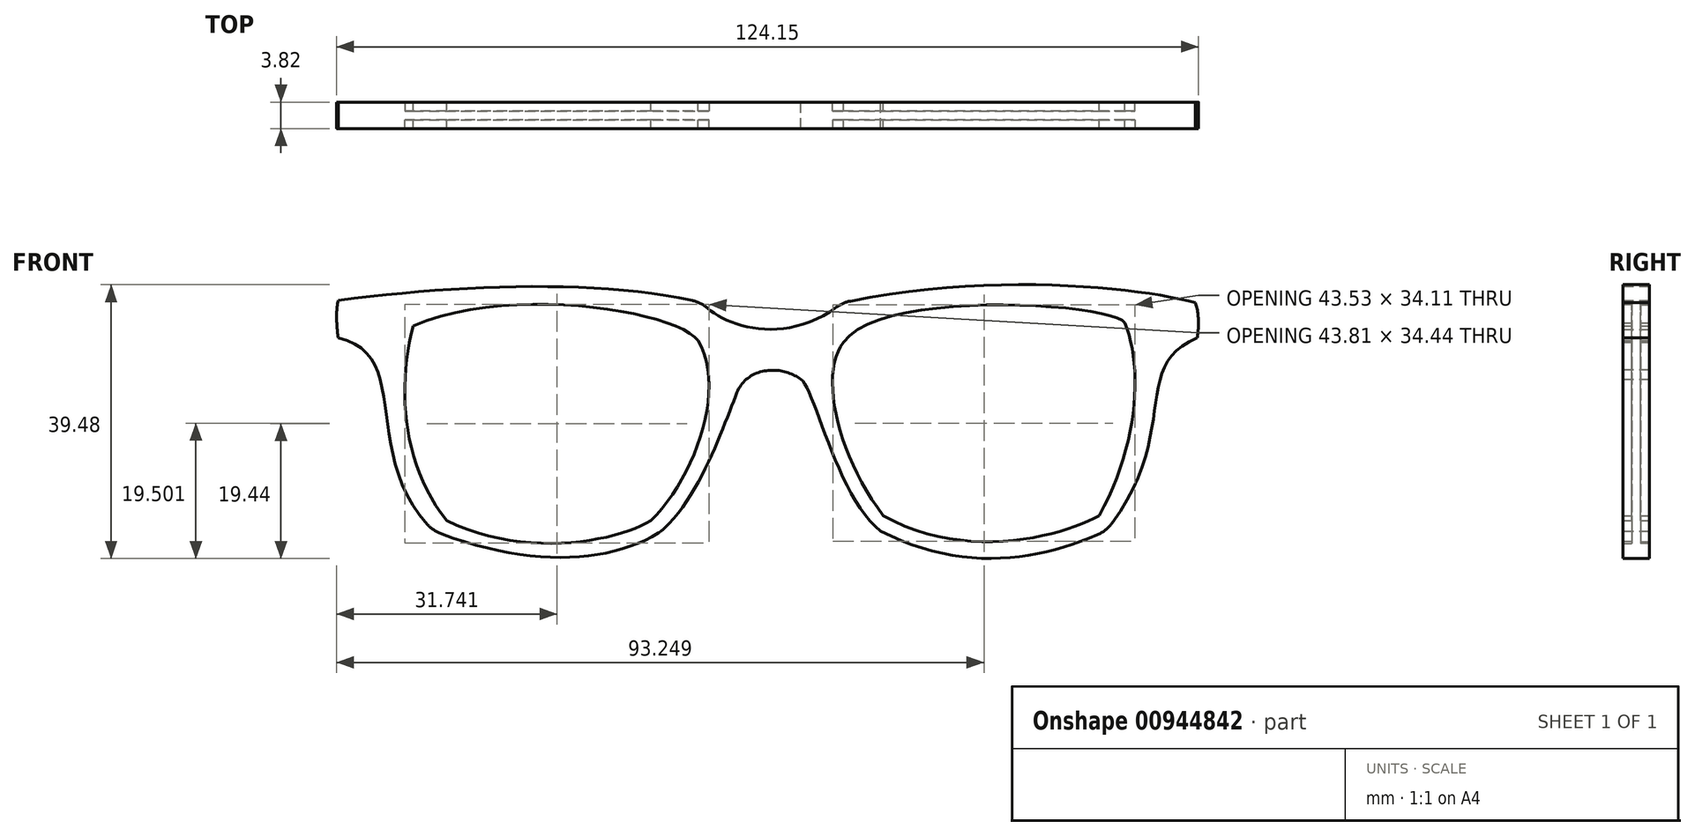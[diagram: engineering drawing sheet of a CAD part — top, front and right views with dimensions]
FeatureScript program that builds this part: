
annotation { "Feature Type Name" : "Feature", "Feature Type Description" : "" }
export const myFeature = defineFeature(function(context is Context, id is Id, definition is map)
    precondition{}
    {
        {
            var Q0;
            Q0=qCreatedBy(makeId("Front.planeOp"),FACE);
            var sketch = newSketch(context, id + "F0", { "sketchPlane" : qUnion([Q0])});
            skFitSpline(sketch, "E0", {"points": [v(-53.61, 9.1) * mm, v(-12.56, 6.99) * mm], "startDerivative": vector(43.48, 18.64) * mm, "endDerivative": vector(8.51, -12.35) * mm});
            skFitSpline(sketch, "E1", {"points": [v(-12.56, 6.99) * mm, v(-19.4, -18.98) * mm], "startDerivative": vector(12.35, -20.96) * mm, "endDerivative": vector(-19.08, -18.72) * mm});
            skFitSpline(sketch, "E2", {"points": [v(-19.4, -18.98) * mm, v(-48.8, -18.98) * mm], "startDerivative": vector(-14.04, -8.75) * mm, "endDerivative": vector(-34.2, 16.69) * mm});
            skFitSpline(sketch, "E3", {"points": [v(-48.8, -18.98) * mm, v(-53.61, 9.1) * mm], "startDerivative": vector(-19.22, 24.46) * mm, "endDerivative": vector(7.01, 27.3) * mm});
            skFitSpline(sketch, "E4", {"points": [v(48.9, 9.56) * mm, v(8.39, 6.78) * mm], "startDerivative": vector(-4.35, 8.37) * mm, "endDerivative": vector(-16.74, -23.44) * mm});
            skFitSpline(sketch, "E5", {"points": [v(8.39, 6.78) * mm, v(14.08, -18.23) * mm], "startDerivative": vector(-10.71, -13.73) * mm, "endDerivative": vector(19.75, -26.45) * mm});
            skFitSpline(sketch, "E6", {"points": [v(14.08, -18.23) * mm, v(45.22, -18.23) * mm], "startDerivative": vector(35.5, -20.09) * mm, "endDerivative": vector(15.8, 8.95) * mm});
            skFitSpline(sketch, "E7", {"points": [v(45.22, -18.23) * mm, v(48.9, 9.56) * mm], "startDerivative": vector(17.04, 30.85) * mm, "endDerivative": vector(-7.8, 18.98) * mm});
            skFitSpline(sketch, "E8", {"points": [v(-64.4, 12.8) * mm, v(-11.95, 12.46) * mm], "startDerivative": vector(54.25, 7.05) * mm, "endDerivative": vector(42.76, -10.3) * mm});
            skFitSpline(sketch, "E9", {"points": [v(-11.95, 12.46) * mm, v(8.2, 12.46) * mm], "startDerivative": vector(8.02, -9.7) * mm, "endDerivative": vector(24.59, 20.06) * mm});
            skFitSpline(sketch, "E10", {"points": [v(8.2, 12.46) * mm, v(59.06, 12.46) * mm], "startDerivative": vector(66.65, 13.92) * mm, "endDerivative": vector(22.94, -6.28) * mm});
            skFitSpline(sketch, "E11", {"points": [v(-64.4, 12.8) * mm, v(-64.4, 7.4) * mm], "startDerivative": vector(-1.17, -5.46) * mm, "endDerivative": vector(0.72, -5.36) * mm});
            skFitSpline(sketch, "E12", {"points": [v(-64.4, 7.4) * mm, v(-50.63, -20.46) * mm], "startDerivative": vector(32.8, -7.15) * mm, "endDerivative": vector(32.63, -31.73) * mm});
            skFitSpline(sketch, "E13", {"points": [v(-50.63, -20.46) * mm, v(-17.86, -20.46) * mm], "startDerivative": vector(41.12, -16.09) * mm, "endDerivative": vector(21.9, 14.3) * mm});
            skFitSpline(sketch, "E14", {"points": [v(-17.86, -20.46) * mm, v(-5.94, 1.44) * mm], "startDerivative": vector(21, 18.32) * mm, "endDerivative": vector(4.6, 4.32) * mm});
            skFitSpline(sketch, "E15", {"points": [v(-5.94, 1.44) * mm, v(2.25, 1.44) * mm], "startDerivative": vector(9.39, 5.81) * mm, "endDerivative": vector(6.76, -4.47) * mm});
            skFitSpline(sketch, "E16", {"points": [v(2.25, 1.44) * mm, v(13.73, -20.46) * mm], "startDerivative": vector(5.9, -4.32) * mm, "endDerivative": vector(18.32, -13.85) * mm});
            skFitSpline(sketch, "E17", {"points": [v(13.73, -20.46) * mm, v(46.2, -20.46) * mm], "startDerivative": vector(36.55, -18.77) * mm, "endDerivative": vector(27.7, 12.51) * mm});
            skFitSpline(sketch, "E18", {"points": [v(46.2, -20.46) * mm, v(59.31, 7.4) * mm], "startDerivative": vector(33.07, 41.56) * mm, "endDerivative": vector(29.5, 12.51) * mm});
            skFitSpline(sketch, "E19", {"points": [v(59.31, 7.4) * mm, v(59.06, 12.46) * mm], "startDerivative": vector(0.9, 4.92) * mm, "endDerivative": vector(-1.64, 4.9) * mm});
            skSolve(sketch);
        }
        {
            var Q0;
            Q0=makeQuery(id+"F0.imprint","IMPRINT",FACE,{"disambiguationData":[TD([[makeQuery(id+"F0.imprint","IMPRINT",EDGE,{"derivedFrom":sQuery(id+"F0.wireOp",EDGE,"E0")}),1.0]])]});
            extrude(context, id + "F1", {"entities" : qUnion([Q0]), "depth" : 3.8 * mm, "offsetDistance" : 25.4 * mm, "symmetric" : true});
        }
        {
            var Q0;
            Q0=makeQuery(id+"F1.opExtrude","SWEPT_EDGE",EDGE,{"disambiguationData":[OSD([sQuery(id+"F0.wireOp",EDGE,"E12"),sQuery(id+"F0.wireOp",EDGE,"E13")])]});
            var Q1;
            Q1=makeQuery(id+"F1.opExtrude","SWEPT_EDGE",EDGE,{"disambiguationData":[OSD([sQuery(id+"F0.wireOp",EDGE,"E13"),sQuery(id+"F0.wireOp",EDGE,"E14")])]});
            var Q2;
            Q2=makeQuery(id+"F1.opExtrude","SWEPT_EDGE",EDGE,{"disambiguationData":[OSD([sQuery(id+"F0.wireOp",EDGE,"E17"),sQuery(id+"F0.wireOp",EDGE,"E18")])]});
            var Q3;
            Q3=makeQuery(id+"F1.opExtrude","SWEPT_EDGE",EDGE,{"disambiguationData":[OSD([sQuery(id+"F0.wireOp",EDGE,"E14"),sQuery(id+"F0.wireOp",EDGE,"E15")])]});
            var Q4;
            Q4=makeQuery(id+"F1.opExtrude","SWEPT_EDGE",EDGE,{"disambiguationData":[OSD([sQuery(id+"F0.wireOp",EDGE,"E8"),sQuery(id+"F0.wireOp",EDGE,"E9")])]});
            var Q5;
            Q5=makeQuery(id+"F1.opExtrude","SWEPT_EDGE",EDGE,{"disambiguationData":[OSD([sQuery(id+"F0.wireOp",EDGE,"E9"),sQuery(id+"F0.wireOp",EDGE,"E10")])]});
            fillet(context, id + "F2", {"entities" : qUnion([Q0, Q1, Q2, Q3, Q4, Q5]), "radius" : 5.08 * mm, "tangentPropagation" : true, "allowEdgeOverflow" : false});
        }
        {
            var Q0;
            Q0=makeQuery(id+"F0.imprint","IMPRINT",FACE,{"disambiguationData":[TD([[makeQuery(id+"F0.imprint","IMPRINT",EDGE,{"derivedFrom":sQuery(id+"F0.wireOp",EDGE,"E0")}),-1.0]])]});
            var Q1;
            Q1=makeQuery(id+"F0.imprint","IMPRINT",FACE,{"disambiguationData":[TD([[makeQuery(id+"F0.imprint","IMPRINT",EDGE,{"derivedFrom":sQuery(id+"F0.wireOp",EDGE,"E4")}),1.0]])]});
            extrude(context, id + "F3", {"entities" : qUnion([Q0, Q1]), "operationType" : NewBodyOperationType.ADD, "depth" : 1.27 * mm, "offsetDistance" : 25.4 * mm, "symmetric" : true});
        }
    });
